# Revit family: Hager-UNIVERS-Surface_mounted-IP30-Without_Cover-With_DIN-NoHosted-CH-en
name_source: partatom
category: Electrical Equipment
units: mm (PartAtom-declared; Revit-internal decimal feet)

## family parameters
Always vertical = Yes
Cut with Voids When Loaded = No
Maintain Annotation Orientation = No
Panel Configuration = Two Columns, Circuits Across
Part Type = Panelboard
Room Calculation Point = No
Round Connector Dimension = Use Diameter
Shared = No
Work Plane-Based = Yes

## types (20) — shared parameters
Code hager = ADD-EC000214_EU
Default Elevation = 1200 mm
EF000003 - Mounting method = Surface mounted/recessed mounted
EF000007 - Colour = White
EF000024 - UV resistant = No
EF000049 - Depth = 165 mm
EF000116 - RAL-number = 9010
EF000118 - With mounting plate = No
EF000218 - Built-in depth = 161 mm  [stored 0.528215 ft]
EF001062 - EMC-version = No
EF001088 - Extension possible = Yes
EF001134 - DIN-rail = Yes
EF004462 - Type of closure = Other
EF005474 - Degree of protection (IP) = IP30
EF006244 - Transparent cover/door = No
EF006306 - With lock = No
EF009212 - Cover model = With notch
EF015776 - Earthing terminal block = Yes
EF015777 - Neutral terminal block = Yes
EF015941 - Signal passing door = No
ETIM class code = EC000214
ETIM class name = Small distribution board
HG000002-With door or cover = No
HG000003-Range = UNIVERS
HG000005-Thickness = 2 mm  [stored 0.00656168 ft]
HG000006-Flush mounted = No
HG000009-Double swing door = No
HG000010-Asymmetric doors = No
HG000011-Empty rows from bottom = No
HG000012-Door swing angle = 90.00°
HG000013-Door on the left = No
HG000014-Door on the right = Yes
HG000015-Clearance visibility = Yes
HG000016-Door 3D visibility = Yes
HG000017-Distance between poles = 18 mm  [stored 0.0590551 ft]
HG000060-RAL-number = 9010
HG000099-Onfly Template ID = 507532
Manufacturer = Hager
Name BIM&CO = Electricity
Name hager = ADD_Enclosures_EC000214
Reference = Template-Enclosure_EU-EC000214
Uniformat = Low Tension Service & Dist.
Uniformat code = D501001
zero-valued in all types: EF001131 - Inner depth, HG000007-Number of empty columns, HG000008-Number of empty rows

## per-type parameters (varying)
| type | BC_METADATA | EF000008 - Width | EF000040 - Height | EF000266 - Number of rows | EF000332 - Built-in height | EF000846 - Built-in width | EF002950 - Width in number of modular spacings | HG000001-Number of columns | HG000004-Manufacturer reference | HGEF000266-Number of rows | HGEF002950-Width in number of modular spacings |
| UNIVERS-Surface_mounted_W550_H1100_D165_24_Modular_Spacing-FWB72T1S | {"ObjectGuid":"b1c97cc8-af4f-4d9d-a920-c2a5727f6108","ModelGuid":"8091068b-d03e-44be-9c19-63d3fb2ce453","VariantGuid":"b4f7dfb4-8530-4ccf-9b72-120ae3343c9d","Revision":"#16","VariantName":"UNIVERS-Surface_mounted_W550_H1100_D165_24_Modular_Spacing-FWB72T1S"} | 550 mm  [stored 1.80446 ft] | 1100 mm | 7 | 1100 mm | 550 mm  [stored 1.80446 ft] | 24 | 2 | FWB72T1S | 7 | 24 |
| UNIVERS-Surface_mounted_W800_H1100_D165_36_Modular_Spacing-FWB73T1S | {"ObjectGuid":"b1c97cc8-af4f-4d9d-a920-c2a5727f6108","ModelGuid":"8091068b-d03e-44be-9c19-63d3fb2ce453","VariantGuid":"a5685973-491c-485a-a9a5-c0b2e36f4710","Revision":"#16","VariantName":"UNIVERS-Surface_mounted_W800_H1100_D165_36_Modular_Spacing-FWB73T1S"} | 800 mm  [stored 2.62467 ft] | 1100 mm | 7 | 1100 mm | 800 mm  [stored 2.62467 ft] | 36 | 3 | FWB73T1S | 7 | 36 |
| UNIVERS-Surface_mounted_W1050_H1100_D165_48_Modular_Spacing-FWB74T1S | {"ObjectGuid":"b1c97cc8-af4f-4d9d-a920-c2a5727f6108","ModelGuid":"8091068b-d03e-44be-9c19-63d3fb2ce453","VariantGuid":"5635260c-1e74-484c-ac20-299fbab4d9a6","Revision":"#16","VariantName":"UNIVERS-Surface_mounted_W1050_H1100_D165_48_Modular_Spacing-FWB74T1S"} | 1050 mm | 1100 mm | 7 | 1100 mm | 1050 mm | 48 | 4 | FWB74T1S | 7 | 48 |
| UNIVERS-Surface_mounted_W300_H500_D165_12_Modular_Spacing-FWB31T1S | {"ObjectGuid":"b1c97cc8-af4f-4d9d-a920-c2a5727f6108","ModelGuid":"8091068b-d03e-44be-9c19-63d3fb2ce453","VariantGuid":"37bec91c-3922-4f32-b47f-124148c4aed0","Revision":"#16","VariantName":"UNIVERS-Surface_mounted_W300_H500_D165_12_Modular_Spacing-FWB31T1S"} | 300 mm | 500 mm  [stored 1.64042 ft] | 3 | 500 mm  [stored 1.64042 ft] | 300 mm | 12 | 1 | FWB31T1S | 3 | 12 |
| UNIVERS-Surface_mounted_W550_H500_D165_24_Modular_Spacing-FWB32T1S | {"ObjectGuid":"b1c97cc8-af4f-4d9d-a920-c2a5727f6108","ModelGuid":"8091068b-d03e-44be-9c19-63d3fb2ce453","VariantGuid":"144f9c70-7dc9-4b6f-8d82-0031222e2a86","Revision":"#16","VariantName":"UNIVERS-Surface_mounted_W550_H500_D165_24_Modular_Spacing-FWB32T1S"} | 550 mm  [stored 1.80446 ft] | 500 mm  [stored 1.64042 ft] | 3 | 500 mm  [stored 1.64042 ft] | 550 mm  [stored 1.80446 ft] | 24 | 2 | FWB32T1S | 3 | 24 |
| UNIVERS-Surface_mounted_W800_H500_D165_36_Modular_Spacing-FWB33T1S | {"ObjectGuid":"b1c97cc8-af4f-4d9d-a920-c2a5727f6108","ModelGuid":"8091068b-d03e-44be-9c19-63d3fb2ce453","VariantGuid":"b6fbfd61-2c6a-45cc-abe1-4b1897e9366d","Revision":"#16","VariantName":"UNIVERS-Surface_mounted_W800_H500_D165_36_Modular_Spacing-FWB33T1S"} | 800 mm  [stored 2.62467 ft] | 500 mm  [stored 1.64042 ft] | 3 | 500 mm  [stored 1.64042 ft] | 800 mm  [stored 2.62467 ft] | 36 | 3 | FWB33T1S | 3 | 36 |
| UNIVERS-Surface_mounted_W1050_H500_D165_48_Modular_Spacing-FWB34T1S | {"ObjectGuid":"b1c97cc8-af4f-4d9d-a920-c2a5727f6108","ModelGuid":"8091068b-d03e-44be-9c19-63d3fb2ce453","VariantGuid":"4e9a9196-85aa-4080-9cdc-05e724c833a1","Revision":"#16","VariantName":"UNIVERS-Surface_mounted_W1050_H500_D165_48_Modular_Spacing-FWB34T1S"} | 1050 mm | 500 mm  [stored 1.64042 ft] | 3 | 500 mm  [stored 1.64042 ft] | 1050 mm | 48 | 4 | FWB34T1S | 3 | 48 |
| UNIVERS-Surface_mounted_W300_H650_D165_12_Modular_Spacing-FWB41T1S | {"ObjectGuid":"b1c97cc8-af4f-4d9d-a920-c2a5727f6108","ModelGuid":"8091068b-d03e-44be-9c19-63d3fb2ce453","VariantGuid":"21fa3619-8b1e-4b10-8f94-95fd95c0e7f1","Revision":"#16","VariantName":"UNIVERS-Surface_mounted_W300_H650_D165_12_Modular_Spacing-FWB41T1S"} | 300 mm | 650 mm  [stored 2.13255 ft] | 4 | 650 mm  [stored 2.13255 ft] | 300 mm | 12 | 1 | FWB41T1S | 4 | 12 |
| UNIVERS-Surface_mounted_W550_H650_D165_24_Modular_Spacing-FWB42T1S | {"ObjectGuid":"b1c97cc8-af4f-4d9d-a920-c2a5727f6108","ModelGuid":"8091068b-d03e-44be-9c19-63d3fb2ce453","VariantGuid":"475adfac-a0f5-4e4f-8925-405c5899e538","Revision":"#16","VariantName":"UNIVERS-Surface_mounted_W550_H650_D165_24_Modular_Spacing-FWB42T1S"} | 550 mm  [stored 1.80446 ft] | 650 mm  [stored 2.13255 ft] | 4 | 650 mm  [stored 2.13255 ft] | 550 mm  [stored 1.80446 ft] | 24 | 2 | FWB42T1S | 4 | 24 |
| UNIVERS-Surface_mounted_W800_H650_D165_36_Modular_Spacing-FWB43T1S | {"ObjectGuid":"b1c97cc8-af4f-4d9d-a920-c2a5727f6108","ModelGuid":"8091068b-d03e-44be-9c19-63d3fb2ce453","VariantGuid":"a8f814ce-27f0-464a-b973-c6403fbd1bbe","Revision":"#16","VariantName":"UNIVERS-Surface_mounted_W800_H650_D165_36_Modular_Spacing-FWB43T1S"} | 800 mm  [stored 2.62467 ft] | 650 mm  [stored 2.13255 ft] | 4 | 650 mm  [stored 2.13255 ft] | 800 mm  [stored 2.62467 ft] | 36 | 3 | FWB43T1S | 4 | 36 |
| UNIVERS-Surface_mounted_W1050_H650_D165_48_Modular_Spacing-FWB44T1S | {"ObjectGuid":"b1c97cc8-af4f-4d9d-a920-c2a5727f6108","ModelGuid":"8091068b-d03e-44be-9c19-63d3fb2ce453","VariantGuid":"4b54a31c-b0d6-4be5-9d2b-5912e7c4098b","Revision":"#16","VariantName":"UNIVERS-Surface_mounted_W1050_H650_D165_48_Modular_Spacing-FWB44T1S"} | 1050 mm | 650 mm  [stored 2.13255 ft] | 4 | 650 mm  [stored 2.13255 ft] | 1050 mm | 48 | 4 | FWB44T1S | 4 | 48 |
| UNIVERS-Surface_mounted_W300_H800_D165_12_Modular_Spacing-FWB51T1S | {"ObjectGuid":"b1c97cc8-af4f-4d9d-a920-c2a5727f6108","ModelGuid":"8091068b-d03e-44be-9c19-63d3fb2ce453","VariantGuid":"42923fdf-3b9d-4abe-bb96-4ce6fe457cf4","Revision":"#16","VariantName":"UNIVERS-Surface_mounted_W300_H800_D165_12_Modular_Spacing-FWB51T1S"} | 300 mm | 800 mm  [stored 2.62467 ft] | 5 | 800 mm  [stored 2.62467 ft] | 300 mm | 12 | 1 | FWB51T1S | 5 | 12 |
| UNIVERS-Surface_mounted_W550_H800_D165_24_Modular_Spacing-FWB52T1S | {"ObjectGuid":"b1c97cc8-af4f-4d9d-a920-c2a5727f6108","ModelGuid":"8091068b-d03e-44be-9c19-63d3fb2ce453","VariantGuid":"e5c3e7a6-3d21-449b-a0db-43ee2547f87c","Revision":"#16","VariantName":"UNIVERS-Surface_mounted_W550_H800_D165_24_Modular_Spacing-FWB52T1S"} | 550 mm  [stored 1.80446 ft] | 800 mm  [stored 2.62467 ft] | 5 | 800 mm  [stored 2.62467 ft] | 550 mm  [stored 1.80446 ft] | 24 | 2 | FWB52T1S | 5 | 24 |
| UNIVERS-Surface_mounted_W800_H800_D165_36_Modular_Spacing-FWB53T1S | {"ObjectGuid":"b1c97cc8-af4f-4d9d-a920-c2a5727f6108","ModelGuid":"8091068b-d03e-44be-9c19-63d3fb2ce453","VariantGuid":"3c641913-3574-41c8-b824-b6ad9b10d9a5","Revision":"#16","VariantName":"UNIVERS-Surface_mounted_W800_H800_D165_36_Modular_Spacing-FWB53T1S"} | 800 mm  [stored 2.62467 ft] | 800 mm  [stored 2.62467 ft] | 5 | 800 mm  [stored 2.62467 ft] | 800 mm  [stored 2.62467 ft] | 36 | 3 | FWB53T1S | 5 | 36 |
| UNIVERS-Surface_mounted_W1050_H800_D165_48_Modular_Spacing-FWB54T1S | {"ObjectGuid":"b1c97cc8-af4f-4d9d-a920-c2a5727f6108","ModelGuid":"8091068b-d03e-44be-9c19-63d3fb2ce453","VariantGuid":"9018d05e-e4de-470e-9bd2-1efe100d5078","Revision":"#16","VariantName":"UNIVERS-Surface_mounted_W1050_H800_D165_48_Modular_Spacing-FWB54T1S"} | 1050 mm | 800 mm  [stored 2.62467 ft] | 5 | 800 mm  [stored 2.62467 ft] | 1050 mm | 48 | 4 | FWB54T1S | 5 | 48 |
| UNIVERS-Surface_mounted_W300_H950_D165_12_Modular_Spacing-FWB61T1S | {"ObjectGuid":"b1c97cc8-af4f-4d9d-a920-c2a5727f6108","ModelGuid":"8091068b-d03e-44be-9c19-63d3fb2ce453","VariantGuid":"5a2ac6ad-45b9-422a-be0f-bbdf1905d09f","Revision":"#16","VariantName":"UNIVERS-Surface_mounted_W300_H950_D165_12_Modular_Spacing-FWB61T1S"} | 300 mm | 950 mm  [stored 3.1168 ft] | 6 | 950 mm  [stored 3.1168 ft] | 300 mm | 12 | 1 | FWB61T1S | 6 | 12 |
| UNIVERS-Surface_mounted_W550_H950_D165_24_Modular_Spacing-FWB62T1S | {"ObjectGuid":"b1c97cc8-af4f-4d9d-a920-c2a5727f6108","ModelGuid":"8091068b-d03e-44be-9c19-63d3fb2ce453","VariantGuid":"7d13b3d6-9f51-4e94-b94d-42a481db5d43","Revision":"#16","VariantName":"UNIVERS-Surface_mounted_W550_H950_D165_24_Modular_Spacing-FWB62T1S"} | 550 mm  [stored 1.80446 ft] | 950 mm  [stored 3.1168 ft] | 6 | 950 mm  [stored 3.1168 ft] | 550 mm  [stored 1.80446 ft] | 24 | 2 | FWB62T1S | 6 | 24 |
| UNIVERS-Surface_mounted_W800_H950_D165_36_Modular_Spacing-FWB63T1S | {"ObjectGuid":"b1c97cc8-af4f-4d9d-a920-c2a5727f6108","ModelGuid":"8091068b-d03e-44be-9c19-63d3fb2ce453","VariantGuid":"caee3f71-5cb2-4cc9-a85b-ed65cd23f3e3","Revision":"#16","VariantName":"UNIVERS-Surface_mounted_W800_H950_D165_36_Modular_Spacing-FWB63T1S"} | 800 mm  [stored 2.62467 ft] | 950 mm  [stored 3.1168 ft] | 6 | 950 mm  [stored 3.1168 ft] | 800 mm  [stored 2.62467 ft] | 36 | 3 | FWB63T1S | 6 | 36 |
| UNIVERS-Surface_mounted_W1050_H950_D165_48_Modular_Spacing-FWB64T1S | {"ObjectGuid":"b1c97cc8-af4f-4d9d-a920-c2a5727f6108","ModelGuid":"8091068b-d03e-44be-9c19-63d3fb2ce453","VariantGuid":"2cb1cb94-13cc-4e1e-89bb-00fc1fdc04ac","Revision":"#16","VariantName":"UNIVERS-Surface_mounted_W1050_H950_D165_48_Modular_Spacing-FWB64T1S"} | 1050 mm | 950 mm  [stored 3.1168 ft] | 6 | 950 mm  [stored 3.1168 ft] | 1050 mm | 48 | 4 | FWB64T1S | 6 | 48 |
| UNIVERS-Surface_mounted_W300_H1100_D165_12_Modular_Spacing-FWB71T1S | {"ObjectGuid":"b1c97cc8-af4f-4d9d-a920-c2a5727f6108","ModelGuid":"8091068b-d03e-44be-9c19-63d3fb2ce453","VariantGuid":"3c8c2eca-3220-4e25-883c-c2ebcdd5769e","Revision":"#16","VariantName":"UNIVERS-Surface_mounted_W300_H1100_D165_12_Modular_Spacing-FWB71T1S"} | 300 mm | 1100 mm | 7 | 1100 mm | 300 mm | 12 | 1 | FWB71T1S | 7 | 12 |

note: [stored X ft] marks values corroborated as IEEE doubles in the binary element streams (Revit-internal decimal feet)

## geometry (parser evidence)
native form markers: Sweep x16
no freeform markers — native parametric forms only
